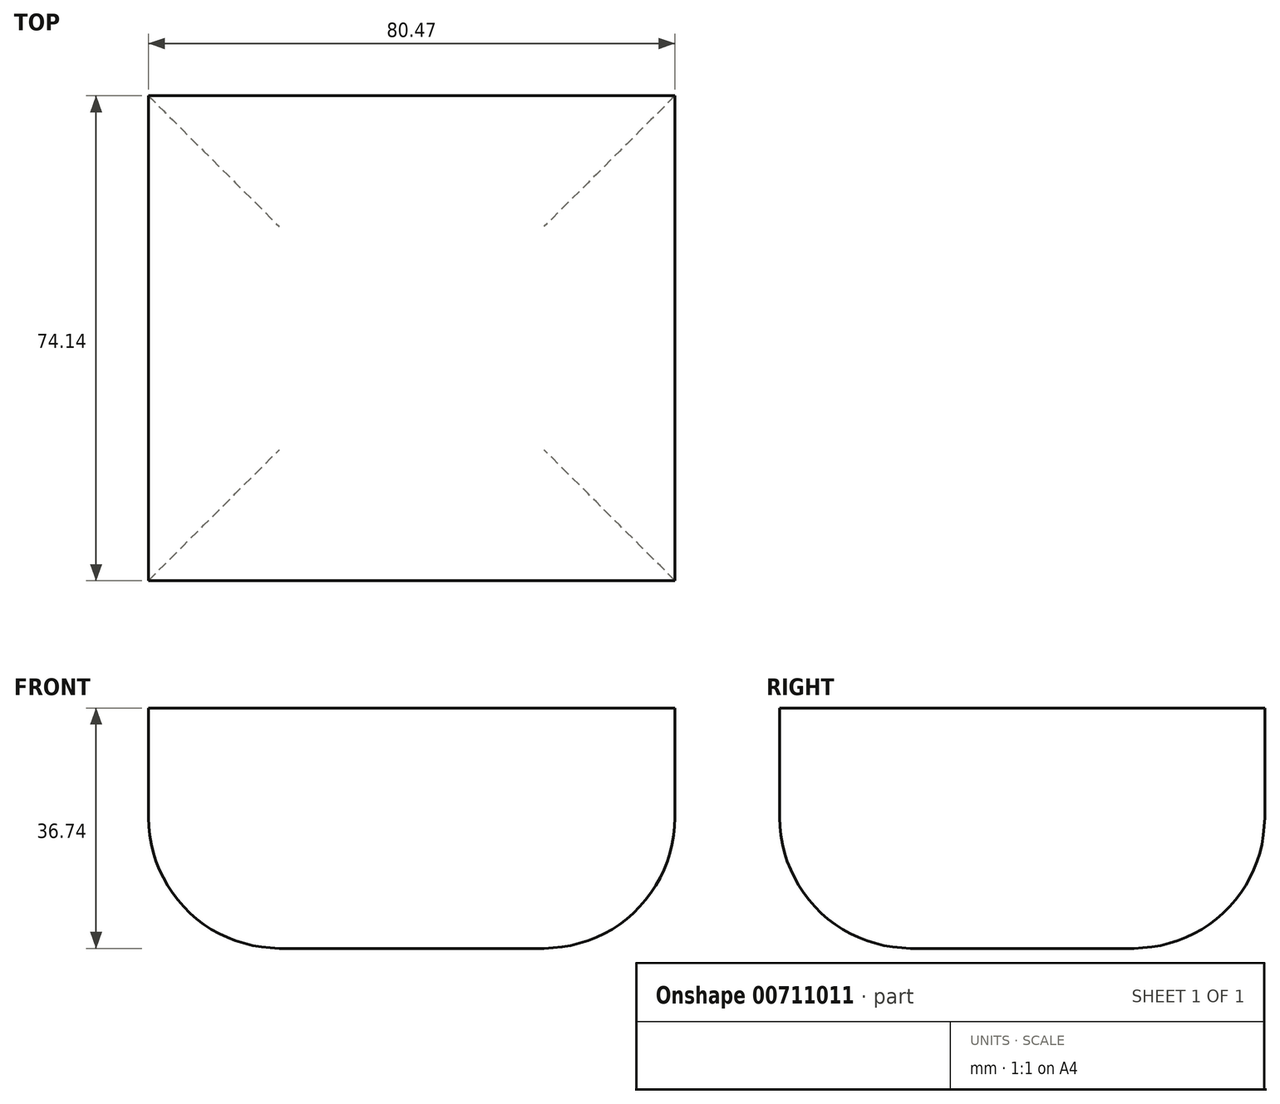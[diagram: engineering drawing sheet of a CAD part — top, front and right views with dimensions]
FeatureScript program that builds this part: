
annotation { "Feature Type Name" : "Feature", "Feature Type Description" : "" }
export const myFeature = defineFeature(function(context is Context, id is Id, definition is map)
    precondition{}
    {
        {
            var Q0;
            Q0=qCreatedBy(makeId("Top.planeOp"),FACE);
            var sketch = newSketch(context, id + "F0", { "sketchPlane" : qUnion([Q0])});
            skLineSegment(sketch, "E0.bottom", {"start": v(41.05, -41.46) * mm, "end": v(-39.42, -41.46) * mm});
            skLineSegment(sketch, "E0.top", {"start": v(41.05, 32.68) * mm, "end": v(-39.42, 32.68) * mm});
            skLineSegment(sketch, "E0.left", {"start": v(41.05, -41.46) * mm, "end": v(41.05, 32.68) * mm});
            skLineSegment(sketch, "E0.right", {"start": v(-39.42, -41.46) * mm, "end": v(-39.42, 32.68) * mm});
            skSolve(sketch);
        }
        {
            var Q0;
            Q0=makeQuery(id+"F0.imprint","IMPRINT",FACE,{"disambiguationData":[TD([[makeQuery(id+"F0.imprint","IMPRINT",EDGE,{"derivedFrom":sQuery(id+"F0.wireOp",EDGE,"E0.bottom")}),-1.0]])]});
            var Q1;
            Q1=sQuery(id+"F0.wireOp",EDGE,"E0.top");
            extrude(context, id + "F1", {"entities" : qUnion([Q0]), "surfaceEntities" : qUnion([Q1]), "endBound" : BoundingType.SYMMETRIC, "depth" : 36.74 * mm, "offsetDistance" : 25.4 * mm});
        }
        {
            var Q0;
            Q0=makeQuery(id+"F1.opExtrude","CAP_EDGE",EDGE,{"disambiguationData":[OSD([sQuery(id+"F0.wireOp",EDGE,"E0.right")])],"isStart":true});
            var Q1;
            Q1=makeQuery(id+"F1.opExtrude","CAP_EDGE",EDGE,{"disambiguationData":[OSD([sQuery(id+"F0.wireOp",EDGE,"E0.top")])],"isStart":true});
            var Q2;
            Q2=makeQuery(id+"F1.opExtrude","CAP_EDGE",EDGE,{"disambiguationData":[OSD([sQuery(id+"F0.wireOp",EDGE,"E0.bottom")])],"isStart":true});
            var Q3;
            Q3=makeQuery(id+"F1.opExtrude","CAP_EDGE",EDGE,{"disambiguationData":[OSD([sQuery(id+"F0.wireOp",EDGE,"E0.left")])],"isStart":true});
            fillet(context, id + "F2", {"entities" : qUnion([Q0, Q1, Q2, Q3]), "radius" : 20 * mm, "tangentPropagation" : true, "allowEdgeOverflow" : false});
        }
    });
